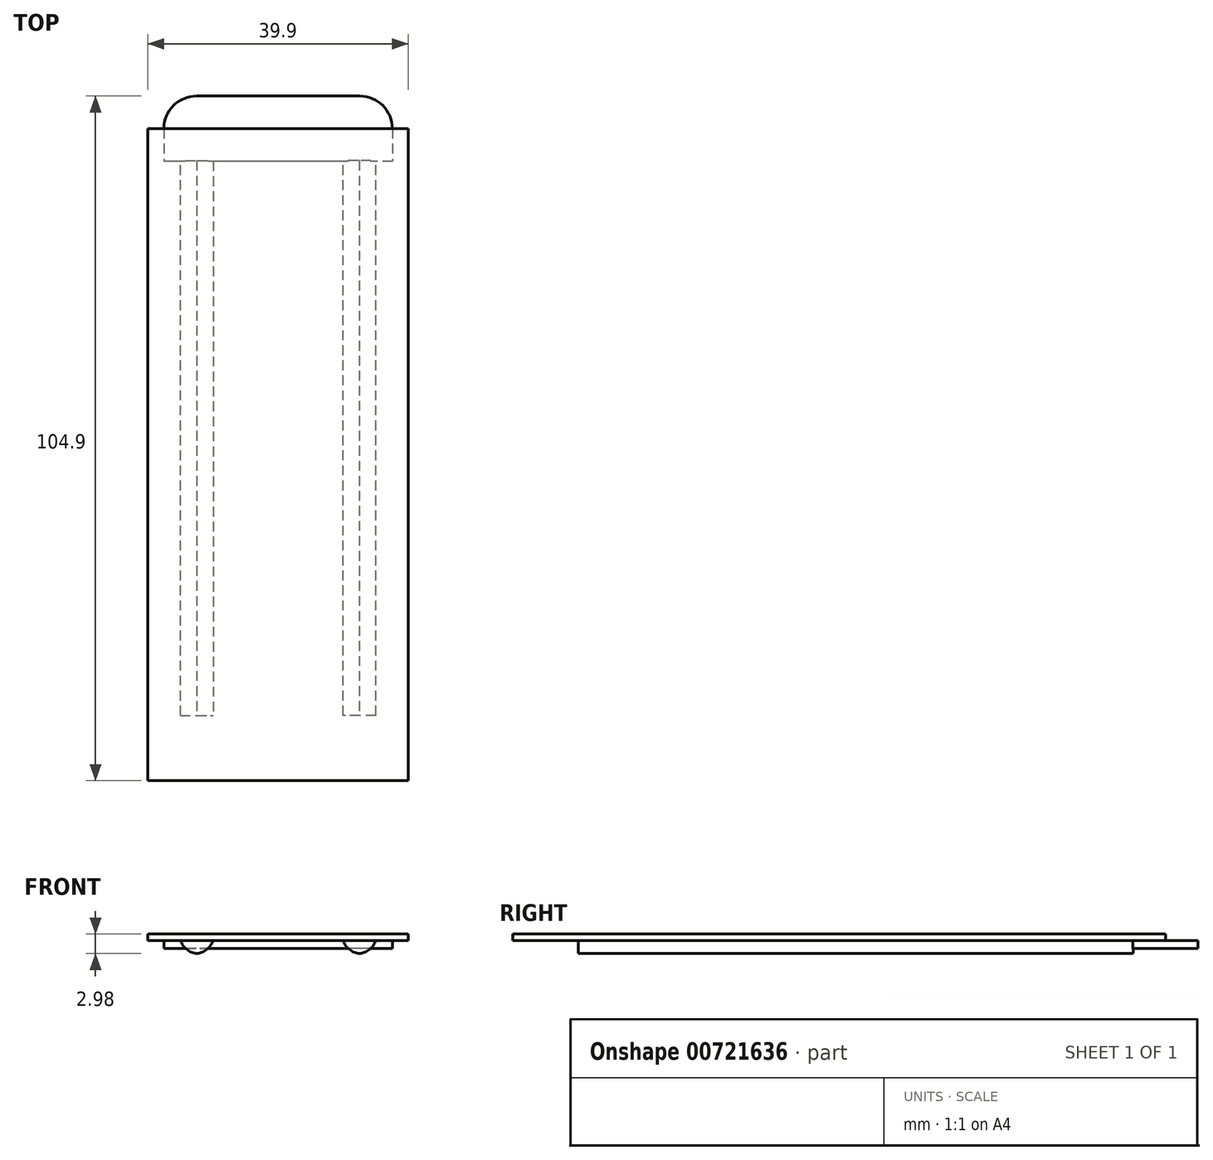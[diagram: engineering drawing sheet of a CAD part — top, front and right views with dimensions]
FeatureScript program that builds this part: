
annotation { "Feature Type Name" : "Feature", "Feature Type Description" : "" }
export const myFeature = defineFeature(function(context is Context, id is Id, definition is map)
    precondition{}
    {
        {
            var Q0;
            Q0=qCreatedBy(makeId("Top.planeOp"),FACE);
            var sketch = newSketch(context, id + "F0", { "sketchPlane" : qUnion([Q0])});
            skLineSegment(sketch, "E0.bottom", {"start": v(19.95, -49.95) * mm, "end": v(-19.95, -49.95) * mm});
            skLineSegment(sketch, "E0.top", {"start": v(19.95, 49.95) * mm, "end": v(-19.95, 49.95) * mm});
            skLineSegment(sketch, "E0.left", {"start": v(19.95, -49.95) * mm, "end": v(19.95, 49.95) * mm});
            skLineSegment(sketch, "E0.right", {"start": v(-19.95, -49.95) * mm, "end": v(-19.95, 49.95) * mm});
            skPoint(sketch, "E0.middle", {"position": v(0, 0) * mm});
            skLineSegment(sketch, "E1.bottom", {"start": v(17.5, 54.95) * mm, "end": v(-17.5, 54.95) * mm});
            skLineSegment(sketch, "E1.top", {"start": v(17.5, 44.95) * mm, "end": v(-17.5, 44.95) * mm});
            skLineSegment(sketch, "E1.left", {"start": v(17.5, 54.95) * mm, "end": v(17.5, 44.95) * mm});
            skLineSegment(sketch, "E1.right", {"start": v(-17.5, 54.95) * mm, "end": v(-17.5, 44.95) * mm});
            skPoint(sketch, "E1.middle", {"position": v(0, 49.95) * mm});
            skSolve(sketch);
        }
        {
            var Q0;
            Q0=makeQuery(id+"F0.imprint","IMPRINT",FACE,{"disambiguationData":[TD([[makeQuery(id+"F0.imprint","IMPRINT",EDGE,{"derivedFrom":sQuery(id+"F0.wireOp",EDGE,"E0.bottom")}),-1.0]])]});
            var Q1;
            {var subQ5=sQuery(id+"F0.wireOp",EDGE,"E1.top");Q1=makeQuery(id+"F0.imprint","IMPRINT",FACE,{"disambiguationData":[TD([[makeQuery(id+"F0.imprint","IMPRINT",EDGE,{"derivedFrom":subQ5}),-1.0]])]});}
            extrude(context, id + "F1", {"entities" : qUnion([Q0, Q1]), "depth" : 1 * mm, "offsetDistance" : 25 * mm});
        }
        {
            var Q0;
            {var subQ5=sQuery(id+"F0.wireOp",EDGE,"E1.bottom");Q0=makeQuery(id+"F0.imprint","IMPRINT",FACE,{"disambiguationData":[TD([[makeQuery(id+"F0.imprint","IMPRINT",EDGE,{"derivedFrom":subQ5}),1.0]])]});}
            var Q1;
            {var subQ5=sQuery(id+"F0.wireOp",EDGE,"E1.top");Q1=makeQuery(id+"F0.imprint","IMPRINT",FACE,{"disambiguationData":[TD([[makeQuery(id+"F0.imprint","IMPRINT",EDGE,{"derivedFrom":subQ5}),-1.0]])]});}
            extrude(context, id + "F2", {"entities" : qUnion([Q0, Q1]), "operationType" : NewBodyOperationType.ADD, "oppositeDirection" : true, "depth" : 1.2 * mm, "offsetDistance" : 25 * mm});
        }
        {
            var Q0;
            Q0=makeQuery(id+"F0.imprint","IMPRINT",FACE,{"disambiguationData":[TD([[makeQuery(id+"F0.imprint","IMPRINT",EDGE,{"derivedFrom":sQuery(id+"F0.wireOp",EDGE,"E0.bottom")}),-1.0]])]});
            var sketch = newSketch(context, id + "F3", { "sketchPlane" : qUnion([Q0])});
            skLineSegment(sketch, "E2.bottom", {"start": v(-14.95, -39.95) * mm, "end": v(-9.95, -39.95) * mm});
            skLineSegment(sketch, "E2.top", {"start": v(-14.95, 45.05) * mm, "end": v(-9.95, 45.05) * mm});
            skLineSegment(sketch, "E2.left", {"start": v(-14.95, -39.95) * mm, "end": v(-14.95, 45.05) * mm});
            skLineSegment(sketch, "E3.bottom", {"start": v(14.95, -39.95) * mm, "end": v(9.95, -39.95) * mm});
            skLineSegment(sketch, "E3.top", {"start": v(14.95, 45.05) * mm, "end": v(9.95, 45.05) * mm});
            skLineSegment(sketch, "E3.left", {"start": v(14.95, -39.95) * mm, "end": v(14.95, 45.05) * mm});
            skLineSegment(sketch, "E4", {"start": v(9.95, -39.95) * mm, "end": v(9.95, 45.05) * mm});
            skLineSegment(sketch, "E5", {"start": v(-9.95, 45.05) * mm, "end": v(-9.95, -39.95) * mm});
            skSolve(sketch);
        }
        {
            var Q0;
            Q0 = qSketchRegion(id + "F3", true);
            extrude(context, id + "F4", {"entities" : qUnion([Q0]), "operationType" : NewBodyOperationType.ADD, "oppositeDirection" : true, "depth" : 2 * mm, "offsetDistance" : 25 * mm});
        }
        {
            var Q0;
            Q0=makeQuery(id+"F4.opExtrude","CAP_EDGE",EDGE,{"disambiguationData":[OSD([sQuery(id+"F3.wireOp",EDGE,"E2.left")])],"isStart":false});
            var Q1;
            Q1=makeQuery(id+"F4.opExtrude","CAP_EDGE",EDGE,{"disambiguationData":[OSD([sQuery(id+"F3.wireOp",EDGE,"E5")])],"isStart":false});
            var Q2;
            Q2=makeQuery(id+"F4.opExtrude","CAP_EDGE",EDGE,{"disambiguationData":[OSD([sQuery(id+"F3.wireOp",EDGE,"E3.left")])],"isStart":false});
            var Q3;
            Q3=makeQuery(id+"F4.opExtrude","CAP_EDGE",EDGE,{"disambiguationData":[OSD([sQuery(id+"F3.wireOp",EDGE,"E4")])],"isStart":false});
            fillet(context, id + "F5", {"entities" : qUnion([Q0, Q1, Q2, Q3]), "radius" : 3 * mm, "tangentPropagation" : true, "allowEdgeOverflow" : false});
        }
        {
            var Q0;
            Q0=makeQuery(id+"F2.opExtrude","SWEPT_EDGE",EDGE,{"disambiguationData":[OSD([sQuery(id+"F0.wireOp",EDGE,"E1.bottom"),sQuery(id+"F0.wireOp",EDGE,"E1.right")])]});
            var Q1;
            Q1=makeQuery(id+"F2.opExtrude","SWEPT_EDGE",EDGE,{"disambiguationData":[OSD([sQuery(id+"F0.wireOp",EDGE,"E1.bottom"),sQuery(id+"F0.wireOp",EDGE,"E1.left")])]});
            fillet(context, id + "F6", {"entities" : qUnion([Q0, Q1]), "radius" : 5 * mm, "tangentPropagation" : true, "allowEdgeOverflow" : false});
        }
    });
